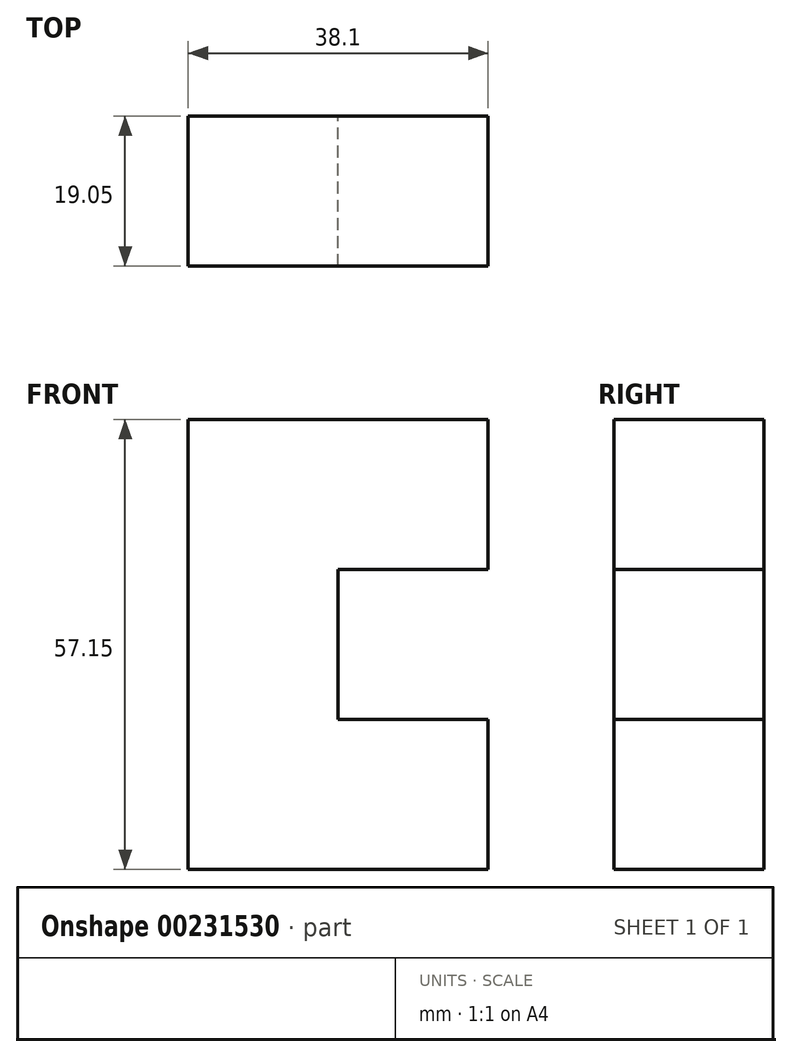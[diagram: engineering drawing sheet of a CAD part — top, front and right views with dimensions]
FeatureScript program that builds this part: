
annotation { "Feature Type Name" : "Feature", "Feature Type Description" : "" }
export const myFeature = defineFeature(function(context is Context, id is Id, definition is map)
    precondition{}
    {
        {
            var Q0;
            Q0=qCreatedBy(makeId("Front.planeOp"),FACE);
            var sketch = newSketch(context, id + "F0", { "sketchPlane" : qUnion([Q0])});
            skLineSegment(sketch, "E0.bottom", {"start": v(-1.71, 31.54) * mm, "end": v(17.34, 31.54) * mm});
            skLineSegment(sketch, "E0.top", {"start": v(-1.71, -25.61) * mm, "end": v(17.34, -25.61) * mm});
            skLineSegment(sketch, "E0.left", {"start": v(-1.71, 31.54) * mm, "end": v(-1.71, -25.61) * mm});
            skLineSegment(sketch, "E0.right", {"start": v(17.34, 31.54) * mm, "end": v(17.34, -25.61) * mm});
            skLineSegment(sketch, "E1.bottom", {"start": v(17.34, 31.54) * mm, "end": v(36.39, 31.54) * mm});
            skLineSegment(sketch, "E1.top", {"start": v(17.34, 12.49) * mm, "end": v(36.39, 12.49) * mm});
            skLineSegment(sketch, "E1.left", {"start": v(17.34, 31.54) * mm, "end": v(17.34, 12.49) * mm});
            skLineSegment(sketch, "E1.right", {"start": v(36.39, 31.54) * mm, "end": v(36.39, 12.49) * mm});
            skLineSegment(sketch, "E2.bottom", {"start": v(17.34, -25.61) * mm, "end": v(36.39, -25.61) * mm});
            skLineSegment(sketch, "E2.top", {"start": v(17.34, -6.56) * mm, "end": v(36.39, -6.56) * mm});
            skLineSegment(sketch, "E2.left", {"start": v(17.34, -25.61) * mm, "end": v(17.34, -6.56) * mm});
            skLineSegment(sketch, "E2.right", {"start": v(36.39, -25.61) * mm, "end": v(36.39, -6.56) * mm});
            skSolve(sketch);
        }
        {
            var Q0;
            Q0 = qSketchRegion(id + "F0", true);
            extrude(context, id + "F1", {"entities" : qUnion([Q0]), "depth" : 19.05 * mm});
        }
    });
